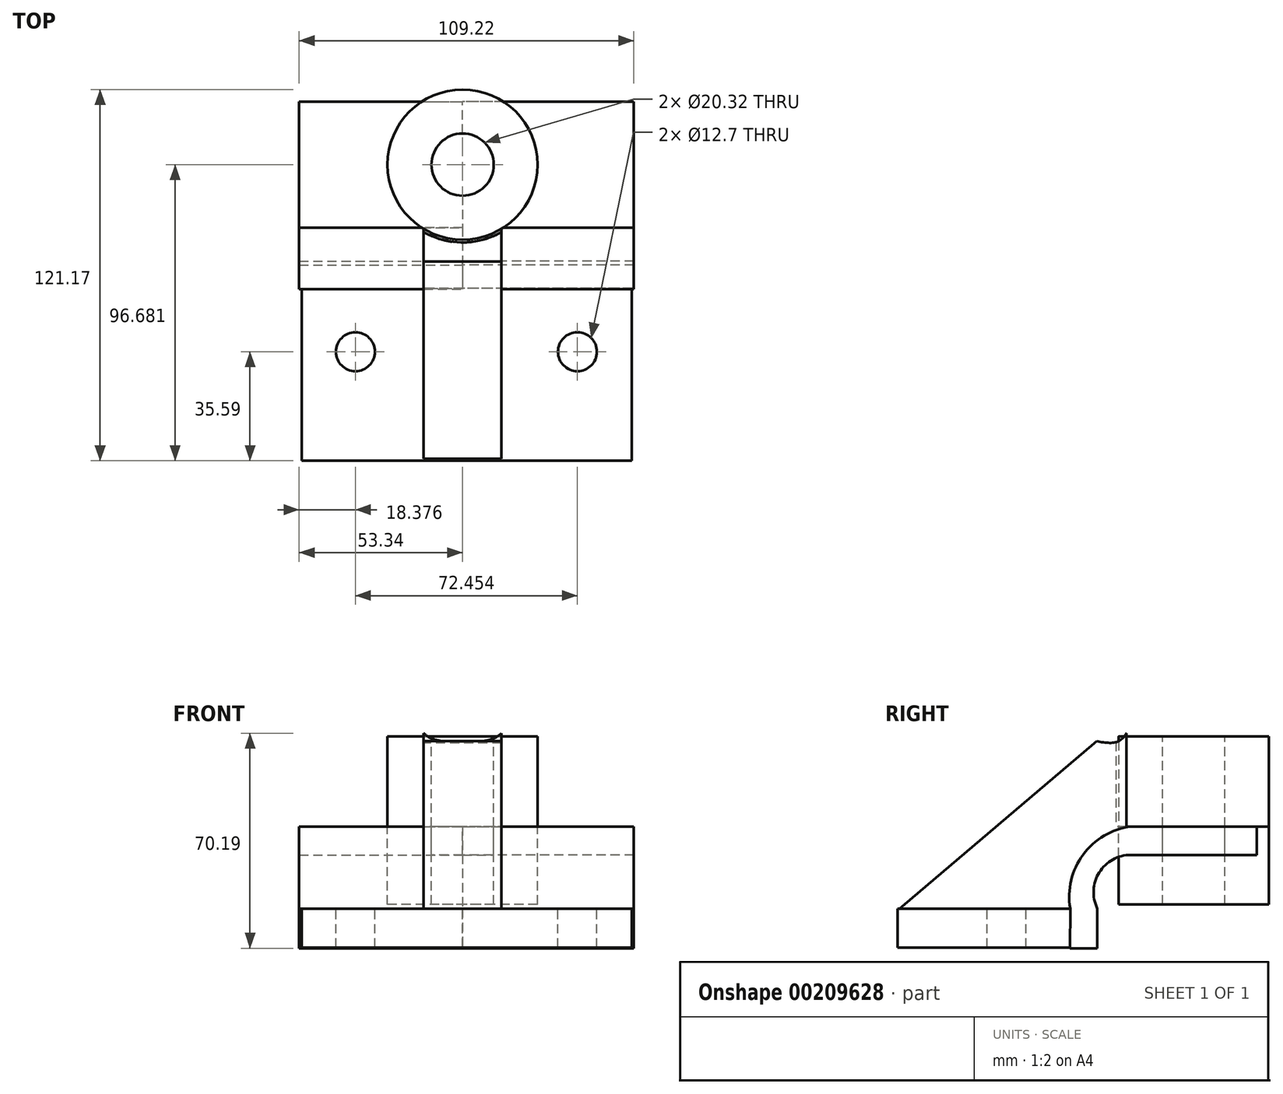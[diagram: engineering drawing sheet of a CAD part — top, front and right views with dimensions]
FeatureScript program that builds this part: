
annotation { "Feature Type Name" : "Feature", "Feature Type Description" : "" }
export const myFeature = defineFeature(function(context is Context, id is Id, definition is map)
    precondition{}
    {
        {
            var Q0;
            Q0=qCreatedBy(makeId("Right.planeOp"),FACE);
            var sketch = newSketch(context, id + "F0", { "sketchPlane" : qUnion([Q0])});
            skLineSegment(sketch, "E0", {"start": v(20.74, 0) * mm, "end": v(-34.98, 0) * mm});
            skLineSegment(sketch, "E1", {"start": v(-34.98, 0) * mm, "end": v(29.4, 54.63) * mm});
            skFitSpline(sketch, "E2", {"points": [v(29.4, 54.63) * mm, v(36.52, 54.63) * mm, v(40.55, 59.9) * mm], "startDerivative": vector(15.46, -2.73) * mm, "endDerivative": vector(6.77, 13.35) * mm});
            skLineSegment(sketch, "E3", {"start": v(40.55, 59.9) * mm, "end": v(40.55, 44.1) * mm});
            skLineSegment(sketch, "E4", {"start": v(40.55, 44.1) * mm, "end": v(40.55, 26.77) * mm});
            skPoint(sketch, "E5.1.internal.orphan", {"position": v(20.74, 22.44) * mm});
            skPoint(sketch, "E5.endDerivative.orphan", {"position": v(36.51, 26.77) * mm});
            skArc(sketch, "E6", {"start": v(40.55, 26.77) * mm, "mid": v(24.95, 17.6) * mm, "end": v(20.74, 0) * mm});
            skLineSegment(sketch, "E7", {"start": v(40.55, 26.77) * mm, "end": v(81.64, 26.77) * mm});
            skLineSegment(sketch, "E8", {"start": v(81.64, 26.77) * mm, "end": v(81.64, 17.52) * mm});
            skLineSegment(sketch, "E9", {"start": v(81.64, 17.52) * mm, "end": v(40.55, 17.52) * mm});
            skArc(sketch, "E10", {"start": v(40.55, 17.52) * mm, "mid": v(30.21, 11.8) * mm, "end": v(29.57, 0) * mm});
            skLineSegment(sketch, "E11", {"start": v(29.57, 0) * mm, "end": v(29.57, -12.96) * mm});
            skLineSegment(sketch, "E12", {"start": v(29.57, -12.96) * mm, "end": v(20.69, -12.96) * mm});
            skLineSegment(sketch, "E13", {"start": v(20.69, -12.96) * mm, "end": v(20.74, 0) * mm});
            skSolve(sketch);
        }
        {
            var Q0;
            Q0=makeQuery(id+"F0.imprint","IMPRINT",FACE,{"disambiguationData":[TD([[makeQuery(id+"F0.imprint","IMPRINT",EDGE,{"derivedFrom":sQuery(id+"F0.wireOp",EDGE,"E0")}),-1.0]])]});
            extrude(context, id + "F1", {"entities" : qUnion([Q0]), "depth" : 12.7 * mm});
        }
        {
            var Q0;
            Q0=makeQuery(id+"F1.opExtrude","CAP_FACE",FACE,{"disambiguationData":[OSD([sQuery(id+"F0.wireOp",EDGE,"E0"),sQuery(id+"F0.wireOp",EDGE,"E1"),sQuery(id+"F0.wireOp",EDGE,"E2"),sQuery(id+"F0.wireOp",EDGE,"E3"),sQuery(id+"F0.wireOp",EDGE,"E4"),sQuery(id+"F0.wireOp",EDGE,"E6")])],"isStart":true});
            extrude(context, id + "F2", {"entities" : qUnion([Q0]), "operationType" : NewBodyOperationType.ADD, "depth" : 12.7 * mm});
        }
        {
            var Q0;
            {var subQ0=sQuery(id+"F0.wireOp",EDGE,"E0");Q0=makeQuery(id+"F2.boolean.opBoolean","MERGE",FACE,{"derivedFrom":[makeQuery(id+"F1.opExtrude","SWEPT_FACE",FACE,{"disambiguationData":[OSD([subQ0])]}),makeQuery(id+"F2.opExtrude","SWEPT_FACE",FACE,{"disambiguationData":[OSD([subQ0])]})]});}
            var sketch = newSketch(context, id + "F3", { "sketchPlane" : qUnion([Q0])});
            skLineSegment(sketch, "E14.bottom", {"start": v(-52.46, -20.74) * mm, "end": v(55.25, -20.74) * mm});
            skLineSegment(sketch, "E14.top", {"start": v(-52.46, 35.6) * mm, "end": v(55.25, 35.6) * mm});
            skLineSegment(sketch, "E14.left", {"start": v(-52.46, -20.74) * mm, "end": v(-52.46, 35.6) * mm});
            skLineSegment(sketch, "E14.right", {"start": v(55.25, -20.74) * mm, "end": v(55.25, 35.6) * mm});
            skSolve(sketch);
        }
        {
            var Q0;
            Q0=makeQuery(id+"F3.imprint","IMPRINT",FACE,{"disambiguationData":[TD([[makeQuery(id+"F3.imprint","IMPRINT",EDGE,{"derivedFrom":sQuery(id+"F3.wireOp",EDGE,"E14.top")}),-1.0]])]});
            var Q1;
            {var subQ1=sQuery(id+"F0.wireOp",EDGE,"E0");var subQ2=makeQuery(id+"F1.opExtrude","CAP_EDGE",EDGE,{"disambiguationData":[OSD([subQ1])],"isStart":false});Q1=makeQuery(id+"F3.imprint","IMPRINT",FACE,{"disambiguationData":[TD([[makeQuery(id+"F3.imprint","IMPRINT",EDGE,{"derivedFrom":subQ2}),1.0]])]});}
            extrude(context, id + "F4", {"entities" : qUnion([Q0, Q1]), "operationType" : NewBodyOperationType.ADD, "depth" : 12.7 * mm});
        }
        {
            var Q0;
            Q0=makeQuery(id+"F4.opExtrude","CAP_FACE",FACE,{"disambiguationData":[OSD([sQuery(id+"F3.wireOp",EDGE,"E14.bottom"),sQuery(id+"F3.wireOp",EDGE,"E14.top"),sQuery(id+"F3.wireOp",EDGE,"E14.left"),sQuery(id+"F3.wireOp",EDGE,"E14.right")])],"isStart":true});
            var sketch = newSketch(context, id + "F5", { "sketchPlane" : qUnion([Q0])});
            skPoint(sketch, "E15", {"position": v(-34.96, 0) * mm});
            skPoint(sketch, "E16", {"position": v(37.5, 0) * mm});
            skSolve(sketch);
        }
        {
            var Q0;
            Q0=sQuery(id+"F5.wireOp",VERTEX,"E15");
            var Q1;
            Q1=sQuery(id+"F5.wireOp",VERTEX,"E16");
            var Q2;
            Q2=makeQuery(id+"F1.opExtrude","SWEPT_BODY",BODY,{"disambiguationData":[OSD([sQuery(id+"F0.wireOp",EDGE,"E0"),sQuery(id+"F0.wireOp",EDGE,"E1"),sQuery(id+"F0.wireOp",EDGE,"E2"),sQuery(id+"F0.wireOp",EDGE,"E3"),sQuery(id+"F0.wireOp",EDGE,"E4"),sQuery(id+"F0.wireOp",EDGE,"E6")])]});
            hole(context, id + "F6", {"style" : HoleStyle.SIMPLE, "endStyle" : HoleEndStyle.THROUGH, "holeDiameter" : 12.7 * mm, "locations" : qUnion([Q0, Q1]), "scope" : qUnion([Q2]), "isTappedThrough" : true});
        }
        {
            var Q0;
            Q0=makeQuery(id+"F0.imprint","IMPRINT",FACE,{"disambiguationData":[TD([[makeQuery(id+"F0.imprint","IMPRINT",EDGE,{"derivedFrom":sQuery(id+"F0.wireOp",EDGE,"E6")}),1.0]])]});
            extrude(context, id + "F7", {"entities" : qUnion([Q0]), "operationType" : NewBodyOperationType.ADD, "depth" : 55.88 * mm});
        }
        {
            var Q0;
            Q0=makeQuery(id+"F0.imprint","IMPRINT",FACE,{"disambiguationData":[TD([[makeQuery(id+"F0.imprint","IMPRINT",EDGE,{"derivedFrom":sQuery(id+"F0.wireOp",EDGE,"E6")}),1.0]])]});
            extrude(context, id + "F8", {"entities" : qUnion([Q0]), "oppositeDirection" : true, "depth" : 53.34 * mm});
        }
        {
            var Q0;
            Q0=makeQuery(id+"F7.opExtrude","SWEPT_FACE",FACE,{"disambiguationData":[OSD([sQuery(id+"F0.wireOp",EDGE,"E7")])]});
            var sketch = newSketch(context, id + "F9", { "sketchPlane" : qUnion([Q0])});
            skPoint(sketch, "E17", {"position": v(0, 61.1) * mm});
            skSolve(sketch);
        }
        {
            var Q0;
            Q0=sQuery(id+"F9.wireOp",VERTEX,"E17");
            var Q1;
            Q1=makeQuery(id+"F1.opExtrude","SWEPT_BODY",BODY,{"disambiguationData":[OSD([sQuery(id+"F0.wireOp",EDGE,"E0"),sQuery(id+"F0.wireOp",EDGE,"E1"),sQuery(id+"F0.wireOp",EDGE,"E2"),sQuery(id+"F0.wireOp",EDGE,"E3"),sQuery(id+"F0.wireOp",EDGE,"E4"),sQuery(id+"F0.wireOp",EDGE,"E6")])]});
            var Q2;
            Q2=makeQuery(id+"F8.opExtrude","SWEPT_BODY",BODY,{"disambiguationData":[OSD([sQuery(id+"F0.wireOp",EDGE,"E6"),sQuery(id+"F0.wireOp",EDGE,"E7"),sQuery(id+"F0.wireOp",EDGE,"E8"),sQuery(id+"F0.wireOp",EDGE,"E9"),sQuery(id+"F0.wireOp",EDGE,"E10"),sQuery(id+"F0.wireOp",EDGE,"E11"),sQuery(id+"F0.wireOp",EDGE,"E12"),sQuery(id+"F0.wireOp",EDGE,"E13")])]});
            hole(context, id + "F10", {"style" : HoleStyle.SIMPLE, "endStyle" : HoleEndStyle.THROUGH, "oppositeDirection" : true, "holeDiameter" : 50.8 * mm, "locations" : qUnion([Q0]), "scope" : qUnion([Q1, Q2]), "isTappedThrough" : true});
        }
        {
            var Q0;
            Q0=makeQuery(id+"F8.opExtrude","SWEPT_FACE",FACE,{"disambiguationData":[OSD([sQuery(id+"F0.wireOp",EDGE,"E7")])]});
            var sketch = newSketch(context, id + "F11", { "sketchPlane" : qUnion([Q0])});
            skCircle(sketch, "E18", {"center": v(0, 61.1) * mm, "radius": 24.5 * mm});
            skSolve(sketch);
        }
        {
            var Q0;
            Q0=makeQuery(id+"F11.imprint","IMPRINT",FACE,{"disambiguationData":[TD([[makeQuery(id+"F11.imprint","IMPRINT",EDGE,{"derivedFrom":sQuery(id+"F11.wireOp",EDGE,"E18")}),1.0]])]});
            extrude(context, id + "F12", {"entities" : qUnion([Q0]), "depth" : 29.46 * mm});
        }
        {
            var Q0;
            Q0=makeQuery(id+"F12.opExtrude","CAP_FACE",FACE,{"disambiguationData":[OSD([sQuery(id+"F11.wireOp",EDGE,"E18")])],"isStart":true});
            extrude(context, id + "F13", {"entities" : qUnion([Q0]), "depth" : 25.4 * mm});
        }
        {
            var Q0;
            Q0=makeQuery(id+"F12.opExtrude","CAP_FACE",FACE,{"disambiguationData":[OSD([sQuery(id+"F11.wireOp",EDGE,"E18")])],"isStart":false});
            var sketch = newSketch(context, id + "F14", { "sketchPlane" : qUnion([Q0])});
            skPoint(sketch, "E19", {"position": v(0, 61.1) * mm});
            skSolve(sketch);
        }
        {
            var Q0;
            Q0=sQuery(id+"F14.wireOp",VERTEX,"E19");
            var Q1;
            Q1=makeQuery(id+"F1.opExtrude","SWEPT_BODY",BODY,{"disambiguationData":[OSD([sQuery(id+"F0.wireOp",EDGE,"E0"),sQuery(id+"F0.wireOp",EDGE,"E1"),sQuery(id+"F0.wireOp",EDGE,"E2"),sQuery(id+"F0.wireOp",EDGE,"E3"),sQuery(id+"F0.wireOp",EDGE,"E4"),sQuery(id+"F0.wireOp",EDGE,"E6")])]});
            var Q2;
            Q2=makeQuery(id+"F8.opExtrude","SWEPT_BODY",BODY,{"disambiguationData":[OSD([sQuery(id+"F0.wireOp",EDGE,"E6"),sQuery(id+"F0.wireOp",EDGE,"E7"),sQuery(id+"F0.wireOp",EDGE,"E8"),sQuery(id+"F0.wireOp",EDGE,"E9"),sQuery(id+"F0.wireOp",EDGE,"E10"),sQuery(id+"F0.wireOp",EDGE,"E11"),sQuery(id+"F0.wireOp",EDGE,"E12"),sQuery(id+"F0.wireOp",EDGE,"E13")])]});
            var Q3;
            Q3=makeQuery(id+"F12.opExtrude","SWEPT_BODY",BODY,{"disambiguationData":[OSD([sQuery(id+"F11.wireOp",EDGE,"E18")])]});
            var Q4;
            Q4=makeQuery(id+"F13.opExtrude","SWEPT_BODY",BODY,{"disambiguationData":[OSD([sQuery(id+"F11.wireOp",EDGE,"E18")])]});
            hole(context, id + "F15", {"style" : HoleStyle.SIMPLE, "endStyle" : HoleEndStyle.THROUGH, "holeDiameter" : 20.32 * mm, "locations" : qUnion([Q0]), "scope" : qUnion([Q1, Q2, Q3, Q4]), "isTappedThrough" : true});
        }
    });
